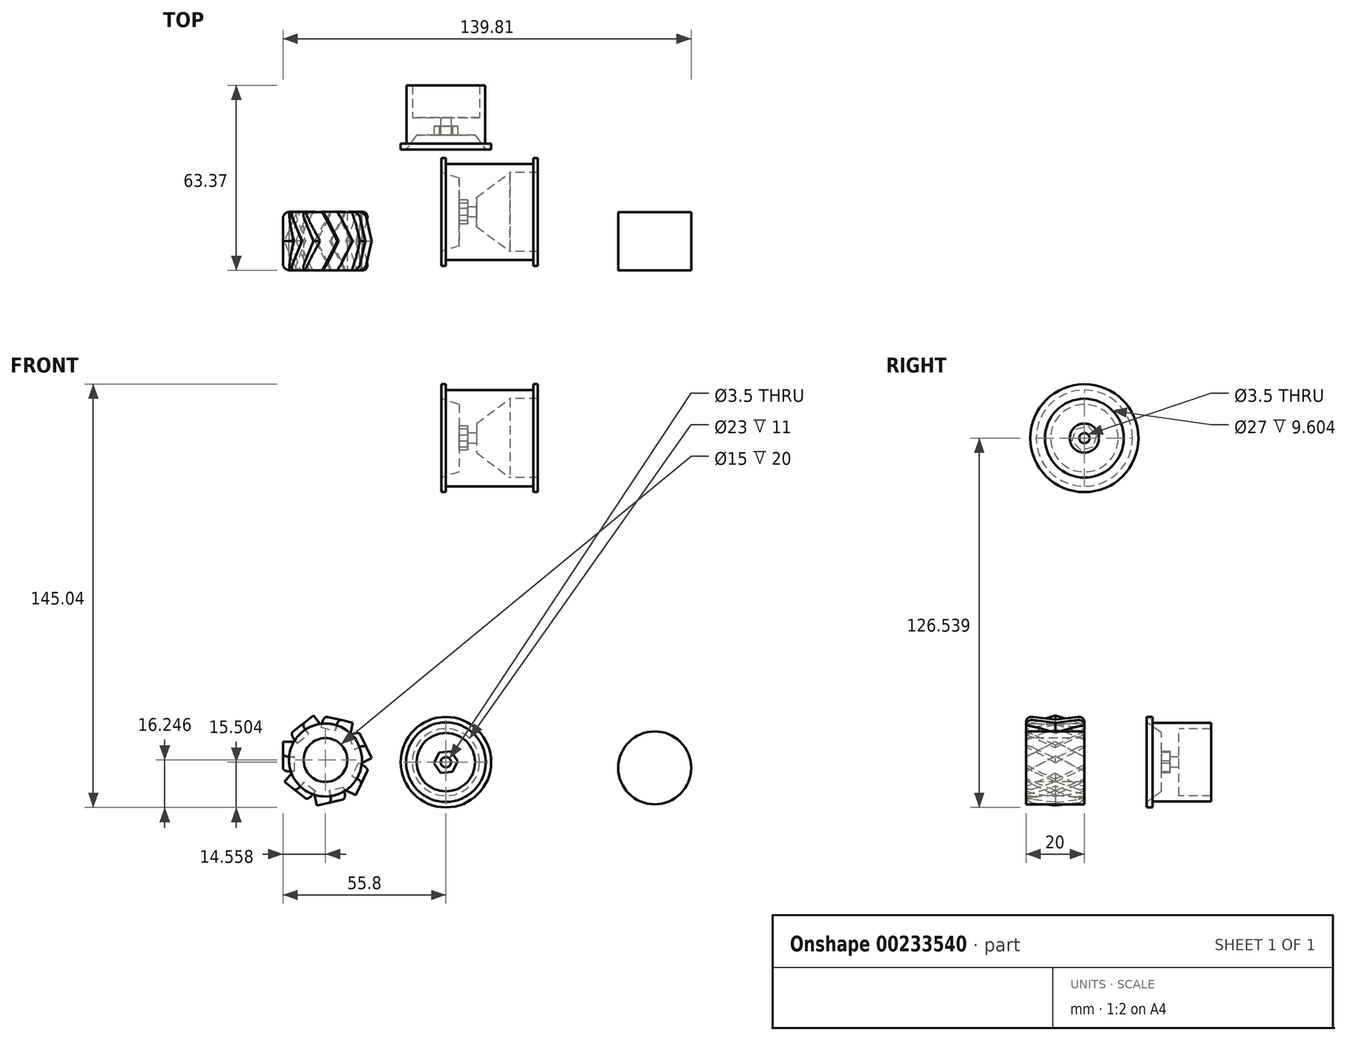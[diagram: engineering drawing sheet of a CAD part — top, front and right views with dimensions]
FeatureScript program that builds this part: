
annotation { "Feature Type Name" : "Feature", "Feature Type Description" : "" }
export const myFeature = defineFeature(function(context is Context, id is Id, definition is map)
    precondition{}
    {
        {
            var Q0;
            Q0=qCreatedBy(makeId("Front.planeOp"),FACE);
            var sketch = newSketch(context, id + "F0", { "sketchPlane" : qUnion([Q0])});
            skCircle(sketch, "E0", {"center": v(-41.24, 29.24) * mm, "radius": 12.5 * mm});
            skSolve(sketch);
        }
        {
            var Q0;
            Q0=qCreatedBy(makeId("Right.planeOp"),FACE);
            var sketch = newSketch(context, id + "F1", { "sketchPlane" : qUnion([Q0])});
            skLineSegment(sketch, "E1", {"start": v(-13.88, 26.8) * mm, "end": v(-23.88, 32.05) * mm});
            skLineSegment(sketch, "E2", {"start": v(-23.88, 32.05) * mm, "end": v(-23.88, 27.05) * mm});
            skLineSegment(sketch, "E3", {"start": v(-23.88, 27.05) * mm, "end": v(-13.88, 21.8) * mm});
            skLineSegment(sketch, "E4", {"start": v(-13.88, 21.8) * mm, "end": v(-13.88, 26.8) * mm});
            skLineSegment(sketch, "E5.MirrorCS", {"start": v(-23.88, 27.05) * mm, "end": v(-33.88, 21.8) * mm});
            skLineSegment(sketch, "E6.MirrorCS", {"start": v(-33.88, 21.8) * mm, "end": v(-33.88, 26.8) * mm});
            skLineSegment(sketch, "E7.MirrorCS", {"start": v(-33.88, 26.8) * mm, "end": v(-23.88, 32.05) * mm});
            skSolve(sketch);
        }
        {
            var Q0;
            Q0=makeQuery(id+"F0.imprint","IMPRINT",FACE,{"disambiguationData":[TD([[makeQuery(id+"F0.imprint","IMPRINT",EDGE,{"derivedFrom":sQuery(id+"F0.wireOp",EDGE,"E0")}),1.0]])]});
            extrude(context, id + "F2", {"entities" : qUnion([Q0]), "depth" : 20 * mm});
        }
        {
            var Q0;
            Q0=makeQuery(id+"F1.imprint","IMPRINT",FACE,{"disambiguationData":[TD([[makeQuery(id+"F1.imprint","IMPRINT",EDGE,{"derivedFrom":sQuery(id+"F1.wireOp",EDGE,"E2")}),-1.0]])]});
            var Q1;
            Q1=makeQuery(id+"F1.imprint","IMPRINT",FACE,{"disambiguationData":[TD([[makeQuery(id+"F1.imprint","IMPRINT",EDGE,{"derivedFrom":sQuery(id+"F1.wireOp",EDGE,"E1")}),1.0]])]});
            extrude(context, id + "F3", {"entities" : qUnion([Q0, Q1]), "depth" : 4 * mm});
        }
        {
            var Q0;
            Q0=makeQuery(id+"F3.opExtrude","SWEPT_BODY",BODY,{"disambiguationData":[OSD([sQuery(id+"F1.wireOp",EDGE,"E1"),sQuery(id+"F1.wireOp",EDGE,"E3"),sQuery(id+"F1.wireOp",EDGE,"E4"),sQuery(id+"F1.wireOp",EDGE,"E5.MirrorCS"),sQuery(id+"F1.wireOp",EDGE,"E6.MirrorCS"),sQuery(id+"F1.wireOp",EDGE,"E7.MirrorCS")])]});
            transform(context, id + "F4", {"entities" : qUnion([Q0]), "transformType" : TransformType.TRANSLATION_3D, "dx" : -55.8 * mm, "dy" : 13.9 * mm, "dz" : 3.5 * mm, "makeCopy" : false});
        }
        {
            var Q0;
            Q0=makeQuery(id+"F3.opExtrude","SWEPT_BODY",BODY,{"disambiguationData":[OSD([sQuery(id+"F1.wireOp",EDGE,"E1"),sQuery(id+"F1.wireOp",EDGE,"E3"),sQuery(id+"F1.wireOp",EDGE,"E4"),sQuery(id+"F1.wireOp",EDGE,"E5.MirrorCS"),sQuery(id+"F1.wireOp",EDGE,"E6.MirrorCS"),sQuery(id+"F1.wireOp",EDGE,"E7.MirrorCS")])]});
            var Q1;
            Q1=makeQuery(id+"F2.opExtrude","CAP_EDGE",EDGE,{"disambiguationData":[OSD([sQuery(id+"F0.wireOp",EDGE,"E0")])],"isStart":true});
            circularPattern(context, id + "F5", {"operationType" : NewBodyOperationType.ADD, "entities" : qUnion([Q0]), "axis" : qUnion([Q1]), "angle" : 360 * degree, "instanceCount" : 7, "equalSpace" : true});
        }
        {
            var Q0;
            Q0=makeQuery(id+"F5.opPattern","COPY",EDGE,{"derivedFrom":makeQuery(id+"F3.opExtrude","CAP_EDGE",EDGE,{"disambiguationData":[OSD([sQuery(id+"F1.wireOp",EDGE,"E4")])],"isStart":true}),"instanceName":"4"});
            var Q1;
            Q1=makeQuery(id+"F5.opPattern","COPY",EDGE,{"derivedFrom":makeQuery(id+"F3.opExtrude","CAP_EDGE",EDGE,{"disambiguationData":[OSD([sQuery(id+"F1.wireOp",EDGE,"E4")])],"isStart":true}),"instanceName":"3"});
            var Q2;
            Q2=makeQuery(id+"F5.opPattern","COPY",EDGE,{"derivedFrom":makeQuery(id+"F3.opExtrude","CAP_EDGE",EDGE,{"disambiguationData":[OSD([sQuery(id+"F1.wireOp",EDGE,"E4")])],"isStart":true}),"instanceName":"2"});
            var Q3;
            Q3=makeQuery(id+"F5.opPattern","COPY",EDGE,{"derivedFrom":makeQuery(id+"F3.opExtrude","CAP_EDGE",EDGE,{"disambiguationData":[OSD([sQuery(id+"F1.wireOp",EDGE,"E4")])],"isStart":true}),"instanceName":"1"});
            var Q4;
            Q4=makeQuery(id+"F3.opExtrude","CAP_EDGE",EDGE,{"disambiguationData":[OSD([sQuery(id+"F1.wireOp",EDGE,"E4")])],"isStart":true});
            var Q5;
            Q5=makeQuery(id+"F5.opPattern","COPY",EDGE,{"derivedFrom":makeQuery(id+"F3.opExtrude","CAP_EDGE",EDGE,{"disambiguationData":[OSD([sQuery(id+"F1.wireOp",EDGE,"E4")])],"isStart":true}),"instanceName":"6"});
            var Q6;
            Q6=makeQuery(id+"F5.opPattern","COPY",EDGE,{"derivedFrom":makeQuery(id+"F3.opExtrude","CAP_EDGE",EDGE,{"disambiguationData":[OSD([sQuery(id+"F1.wireOp",EDGE,"E4")])],"isStart":true}),"instanceName":"5"});
            fillet(context, id + "F6", {"entities" : qUnion([Q0, Q1, Q2, Q3, Q4, Q5, Q6]), "radius" : 2.25 * mm, "tangentPropagation" : true, "allowEdgeOverflow" : false});
        }
        {
            var Q0;
            Q0=makeQuery(id+"F5.opPattern","COPY",EDGE,{"derivedFrom":makeQuery(id+"F3.opExtrude","CAP_EDGE",EDGE,{"disambiguationData":[OSD([sQuery(id+"F1.wireOp",EDGE,"E6.MirrorCS")])],"isStart":true}),"instanceName":"4"});
            var Q1;
            Q1=makeQuery(id+"F5.opPattern","COPY",EDGE,{"derivedFrom":makeQuery(id+"F3.opExtrude","CAP_EDGE",EDGE,{"disambiguationData":[OSD([sQuery(id+"F1.wireOp",EDGE,"E6.MirrorCS")])],"isStart":true}),"instanceName":"5"});
            var Q2;
            Q2=makeQuery(id+"F5.opPattern","COPY",EDGE,{"derivedFrom":makeQuery(id+"F3.opExtrude","CAP_EDGE",EDGE,{"disambiguationData":[OSD([sQuery(id+"F1.wireOp",EDGE,"E6.MirrorCS")])],"isStart":true}),"instanceName":"6"});
            var Q3;
            Q3=makeQuery(id+"F3.opExtrude","CAP_EDGE",EDGE,{"disambiguationData":[OSD([sQuery(id+"F1.wireOp",EDGE,"E6.MirrorCS")])],"isStart":true});
            var Q4;
            Q4=makeQuery(id+"F5.opPattern","COPY",EDGE,{"derivedFrom":makeQuery(id+"F3.opExtrude","CAP_EDGE",EDGE,{"disambiguationData":[OSD([sQuery(id+"F1.wireOp",EDGE,"E6.MirrorCS")])],"isStart":true}),"instanceName":"1"});
            var Q5;
            Q5=makeQuery(id+"F5.opPattern","COPY",EDGE,{"derivedFrom":makeQuery(id+"F3.opExtrude","CAP_EDGE",EDGE,{"disambiguationData":[OSD([sQuery(id+"F1.wireOp",EDGE,"E6.MirrorCS")])],"isStart":true}),"instanceName":"2"});
            var Q6;
            Q6=makeQuery(id+"F5.opPattern","COPY",EDGE,{"derivedFrom":makeQuery(id+"F3.opExtrude","CAP_EDGE",EDGE,{"disambiguationData":[OSD([sQuery(id+"F1.wireOp",EDGE,"E6.MirrorCS")])],"isStart":true}),"instanceName":"3"});
            fillet(context, id + "F7", {"entities" : qUnion([Q0, Q1, Q2, Q3, Q4, Q5, Q6]), "radius" : 2.25 * mm, "tangentPropagation" : true, "allowEdgeOverflow" : false});
        }
        {
            var Q0;
            Q0=makeQuery(id+"F2.opExtrude","CAP_FACE",FACE,{"disambiguationData":[OSD([sQuery(id+"F0.wireOp",EDGE,"E0")])],"isStart":false});
            var sketch = newSketch(context, id + "F8", { "sketchPlane" : qUnion([Q0])});
            skCircle(sketch, "E8", {"center": v(-41.24, 29.24) * mm, "radius": 7.5 * mm});
            skSolve(sketch);
        }
        {
            var Q0;
            Q0=makeQuery(id+"F8.imprint","IMPRINT",FACE,{"disambiguationData":[TD([[makeQuery(id+"F8.imprint","IMPRINT",EDGE,{"derivedFrom":sQuery(id+"F8.wireOp",EDGE,"E8")}),1.0]])]});
            var Q1;
            Q1=sQuery(id+"F8.wireOp",EDGE,"E8");
            extrude(context, id + "F9", {"entities" : qUnion([Q0]), "operationType" : NewBodyOperationType.REMOVE, "surfaceEntities" : qUnion([Q1]), "endBound" : BoundingType.THROUGH_ALL, "oppositeDirection" : true, "depth" : 25 * mm});
        }
        {
            var Q0;
            Q0=qCreatedBy(makeId("Front.planeOp"),FACE);
            var sketch = newSketch(context, id + "F10", { "sketchPlane" : qUnion([Q0])});
            skCircle(sketch, "E9", {"center": v(71.51, 26.54) * mm, "radius": 12.5 * mm});
            skSolve(sketch);
        }
        {
            var Q0;
            Q0=makeQuery(id+"F10.imprint","IMPRINT",FACE,{"disambiguationData":[TD([[makeQuery(id+"F10.imprint","IMPRINT",EDGE,{"derivedFrom":sQuery(id+"F10.wireOp",EDGE,"E9")}),1.0]])]});
            extrude(context, id + "F11", {"entities" : qUnion([Q0]), "depth" : 20 * mm});
        }
        {
            var Q0;
            Q0=qCreatedBy(makeId("Front.planeOp"),FACE);
            var sketch = newSketch(context, id + "F12", { "sketchPlane" : qUnion([Q0])});
            skLineSegment(sketch, "E10", {"start": v(-1.5, 121.03) * mm, "end": v(0, 121.03) * mm});
            skLineSegment(sketch, "E11", {"start": v(0, 121.03) * mm, "end": v(0, 123.03) * mm});
            skLineSegment(sketch, "E12", {"start": v(0, 123.03) * mm, "end": v(30, 123.03) * mm});
            skLineSegment(sketch, "E13", {"start": v(30, 123.03) * mm, "end": v(30, 121.03) * mm});
            skLineSegment(sketch, "E14", {"start": v(30, 121.03) * mm, "end": v(31.5, 121.03) * mm});
            skLineSegment(sketch, "E15", {"start": v(31.5, 121.03) * mm, "end": v(31.5, 158.03) * mm});
            skLineSegment(sketch, "E16", {"start": v(31.5, 158.03) * mm, "end": v(30, 158.03) * mm});
            skLineSegment(sketch, "E17", {"start": v(30, 158.03) * mm, "end": v(30, 156.03) * mm});
            skLineSegment(sketch, "E18", {"start": v(30, 156.03) * mm, "end": v(0, 156.03) * mm});
            skLineSegment(sketch, "E19", {"start": v(0, 156.03) * mm, "end": v(0, 158.03) * mm});
            skLineSegment(sketch, "E20", {"start": v(0, 158.03) * mm, "end": v(-1.5, 158.03) * mm});
            skLineSegment(sketch, "E21", {"start": v(-1.5, 158.03) * mm, "end": v(-1.5, 121.03) * mm});
            skLineSegment(sketch, "E22", {"start": v(-1.5, 139.53) * mm, "end": v(31.5, 139.53) * mm});
            skLineSegment(sketch, "E23", {"start": v(31.5, 126.03) * mm, "end": v(-1.5, 126.03) * mm});
            skLineSegment(sketch, "E24", {"start": v(10.5, 139.53) * mm, "end": v(10.5, 134.53) * mm});
            skLineSegment(sketch, "E25", {"start": v(10.5, 134.53) * mm, "end": v(21.9, 126.03) * mm});
            skLineSegment(sketch, "E26", {"start": v(-1.5, 126.03) * mm, "end": v(4.5, 127.96) * mm});
            skLineSegment(sketch, "E27", {"start": v(4.5, 127.96) * mm, "end": v(4.5, 139.53) * mm});
            skSolve(sketch);
        }
        {
            var Q0;
            {var subQ4=sQuery(id+"F12.wireOp",EDGE,"E24");Q0=makeQuery(id+"F12.imprint","IMPRINT",FACE,{"disambiguationData":[TD([[makeQuery(id+"F12.imprint","IMPRINT",EDGE,{"derivedFrom":subQ4}),-1.0]])]});}
            var Q1;
            {var subQ0=sQuery(id+"F12.wireOp",EDGE,"E10");Q1=makeQuery(id+"F12.imprint","IMPRINT",FACE,{"disambiguationData":[TD([[makeQuery(id+"F12.imprint","IMPRINT",EDGE,{"derivedFrom":subQ0}),1.0]])]});}
            var Q2;
            Q2=sQuery(id+"F12.wireOp",EDGE,"E22");
            revolve(context, id + "F13", {"entities" : qUnion([Q0, Q1]), "axis" : qUnion([Q2]), "revolveType" : RevolveType.FULL});
        }
        {
            var Q0;
            Q0=makeQuery(id+"F13.opRevolve","SWEPT_FACE",FACE,{"disambiguationData":[OSD([sQuery(id+"F12.wireOp",EDGE,"E21")])]});
            var sketch = newSketch(context, id + "F14", { "sketchPlane" : qUnion([Q0])});
            skCircle(sketch, "E28", {"center": v(0, 139.53) * mm, "radius": 1.75 * mm});
            skCircle(sketch, "E29.cCircle", {"center": v(0, 139.53) * mm, "radius": 3.7 * mm, "construction": true});
            skLineSegment(sketch, "E29.0", {"start": v(1.2, 135.43) * mm, "end": v(-2.95, 136.44) * mm});
            skLineSegment(sketch, "E29.1", {"start": v(-2.95, 136.44) * mm, "end": v(-4.15, 140.54) * mm});
            skLineSegment(sketch, "E29.2", {"start": v(-4.15, 140.54) * mm, "end": v(-1.2, 143.63) * mm});
            skLineSegment(sketch, "E29.3", {"start": v(-1.2, 143.63) * mm, "end": v(2.95, 142.62) * mm});
            skLineSegment(sketch, "E29.4", {"start": v(2.95, 142.62) * mm, "end": v(4.15, 138.52) * mm});
            skLineSegment(sketch, "E29.5", {"start": v(4.15, 138.52) * mm, "end": v(1.2, 135.43) * mm});
            skPoint(sketch, "E29.0.midPoint", {"position": v(-0.88, 135.93) * mm});
            skSolve(sketch);
        }
        {
            var Q0;
            Q0=makeQuery(id+"F14.imprint","IMPRINT",FACE,{"disambiguationData":[TD([[makeQuery(id+"F14.imprint","IMPRINT",EDGE,{"derivedFrom":sQuery(id+"F14.wireOp",EDGE,"E28")}),1.0]])]});
            extrude(context, id + "F15", {"entities" : qUnion([Q0]), "operationType" : NewBodyOperationType.REMOVE, "endBound" : BoundingType.THROUGH_ALL, "oppositeDirection" : true, "depth" : 25 * mm});
        }
        {
            var Q0;
            Q0=makeQuery(id+"F14.imprint","IMPRINT",FACE,{"disambiguationData":[TD([[makeQuery(id+"F14.imprint","IMPRINT",EDGE,{"derivedFrom":sQuery(id+"F14.wireOp",EDGE,"E28")}),-1.0]])]});
            extrude(context, id + "F16", {"entities" : qUnion([Q0]), "operationType" : NewBodyOperationType.REMOVE, "oppositeDirection" : true, "depth" : 3 * mm});
        }
        {
            var Q0;
            Q0=makeQuery(id+"F14.imprint","IMPRINT",FACE,{"disambiguationData":[TD([[makeQuery(id+"F14.imprint","IMPRINT",EDGE,{"derivedFrom":sQuery(id+"F14.wireOp",EDGE,"E28")}),-1.0]])]});
            extrude(context, id + "F17", {"entities" : qUnion([Q0]), "operationType" : NewBodyOperationType.REMOVE, "oppositeDirection" : true, "depth" : 9 * mm});
        }
        {
            var Q0;
            Q0=qCreatedBy(makeId("Right.planeOp"),FACE);
            var sketch = newSketch(context, id + "F18", { "sketchPlane" : qUnion([Q0])});
            skLineSegment(sketch, "E30", {"start": v(21.37, 13) * mm, "end": v(21.37, 14.85) * mm});
            skLineSegment(sketch, "E31", {"start": v(21.37, 14.85) * mm, "end": v(26.37, 18.5) * mm});
            skLineSegment(sketch, "E32", {"start": v(26.37, 18.5) * mm, "end": v(26.37, 28.5) * mm});
            skLineSegment(sketch, "E33", {"start": v(26.37, 28.5) * mm, "end": v(43.37, 28.5) * mm});
            skLineSegment(sketch, "E34", {"start": v(43.37, 28.5) * mm, "end": v(43.37, 15) * mm});
            skLineSegment(sketch, "E35", {"start": v(43.37, 15) * mm, "end": v(23.37, 15) * mm});
            skLineSegment(sketch, "E36", {"start": v(23.37, 15) * mm, "end": v(23.37, 13) * mm});
            skLineSegment(sketch, "E37", {"start": v(23.37, 13) * mm, "end": v(21.37, 13) * mm});
            skLineSegment(sketch, "E38", {"start": v(32.37, 28.5) * mm, "end": v(32.37, 17) * mm});
            skLineSegment(sketch, "E39", {"start": v(32.37, 17) * mm, "end": v(43.37, 17) * mm});
            skLineSegment(sketch, "E40", {"start": v(43.37, 17) * mm, "end": v(43.37, 15) * mm});
            skSolve(sketch);
        }
        {
            var Q0;
            Q0=makeQuery(id+"F18.imprint","IMPRINT",FACE,{"disambiguationData":[TD([[makeQuery(id+"F18.imprint","IMPRINT",EDGE,{"derivedFrom":sQuery(id+"F18.wireOp",EDGE,"E30")}),-1.0]])]});
            var Q1;
            Q1=sQuery(id+"F18.wireOp",EDGE,"E33");
            revolve(context, id + "F19", {"entities" : qUnion([Q0]), "axis" : qUnion([Q1]), "revolveType" : RevolveType.FULL});
        }
        {
            var Q0;
            Q0=makeQuery(id+"F19.opRevolve","SWEPT_FACE",FACE,{"disambiguationData":[OSD([sQuery(id+"F18.wireOp",EDGE,"E32")])]});
            var sketch = newSketch(context, id + "F20", { "sketchPlane" : qUnion([Q0])});
            skCircle(sketch, "E41", {"center": v(0, 28.5) * mm, "radius": 1.75 * mm});
            skCircle(sketch, "E42.cCircle", {"center": v(0, 28.5) * mm, "radius": 3.5 * mm, "construction": true});
            skLineSegment(sketch, "E42.0", {"start": v(4.03, 28.82) * mm, "end": v(2.3, 25.17) * mm});
            skLineSegment(sketch, "E42.1", {"start": v(2.3, 25.17) * mm, "end": v(-1.73, 24.84) * mm});
            skLineSegment(sketch, "E42.2", {"start": v(-1.73, 24.84) * mm, "end": v(-4.03, 28.17) * mm});
            skLineSegment(sketch, "E42.3", {"start": v(-4.03, 28.17) * mm, "end": v(-2.3, 31.82) * mm});
            skLineSegment(sketch, "E42.4", {"start": v(-2.3, 31.82) * mm, "end": v(1.73, 32.15) * mm});
            skLineSegment(sketch, "E42.5", {"start": v(1.73, 32.15) * mm, "end": v(4.03, 28.82) * mm});
            skPoint(sketch, "E42.0.midPoint", {"position": v(3.16, 27) * mm});
            skSolve(sketch);
        }
        {
            var Q0;
            Q0=makeQuery(id+"F20.imprint","IMPRINT",FACE,{"disambiguationData":[TD([[makeQuery(id+"F20.imprint","IMPRINT",EDGE,{"derivedFrom":sQuery(id+"F20.wireOp",EDGE,"E41")}),1.0]])]});
            extrude(context, id + "F21", {"entities" : qUnion([Q0]), "operationType" : NewBodyOperationType.REMOVE, "oppositeDirection" : true, "depth" : 25 * mm});
        }
        {
            var Q0;
            Q0=makeQuery(id+"F20.imprint","IMPRINT",FACE,{"disambiguationData":[TD([[makeQuery(id+"F20.imprint","IMPRINT",EDGE,{"derivedFrom":sQuery(id+"F20.wireOp",EDGE,"E41")}),-1.0]])]});
            extrude(context, id + "F22", {"entities" : qUnion([Q0]), "operationType" : NewBodyOperationType.REMOVE, "oppositeDirection" : true, "depth" : 3 * mm});
        }
    });
